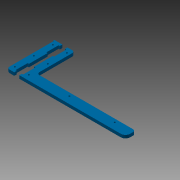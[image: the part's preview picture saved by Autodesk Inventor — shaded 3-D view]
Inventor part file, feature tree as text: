
AUTODESK INVENTOR PART (.ipt)
format: ipt  version: 2013 (Build 170138000, 138)  size: 125,952 bytes
history: native  units: mm
features: extrude x1, sketch x1
ambient origin geometry x8: Origin, YZ Plane, XZ Plane, XY Plane, X Axis, Y Axis, Z Axis, Center Point
bodies: Solid1 (feature_tree)
feature tree (2):
  extrude  "Extrusion1"  [1 undecoded]
  sketch  "Sketch1"  dims[d0=6.0mm d1=0.0mm]
note: 1 required parameter value undecoded (feature->parameter linkage not recoverable at this tier; creation-order binding heuristic only, values carry confidence <= 0.55)
